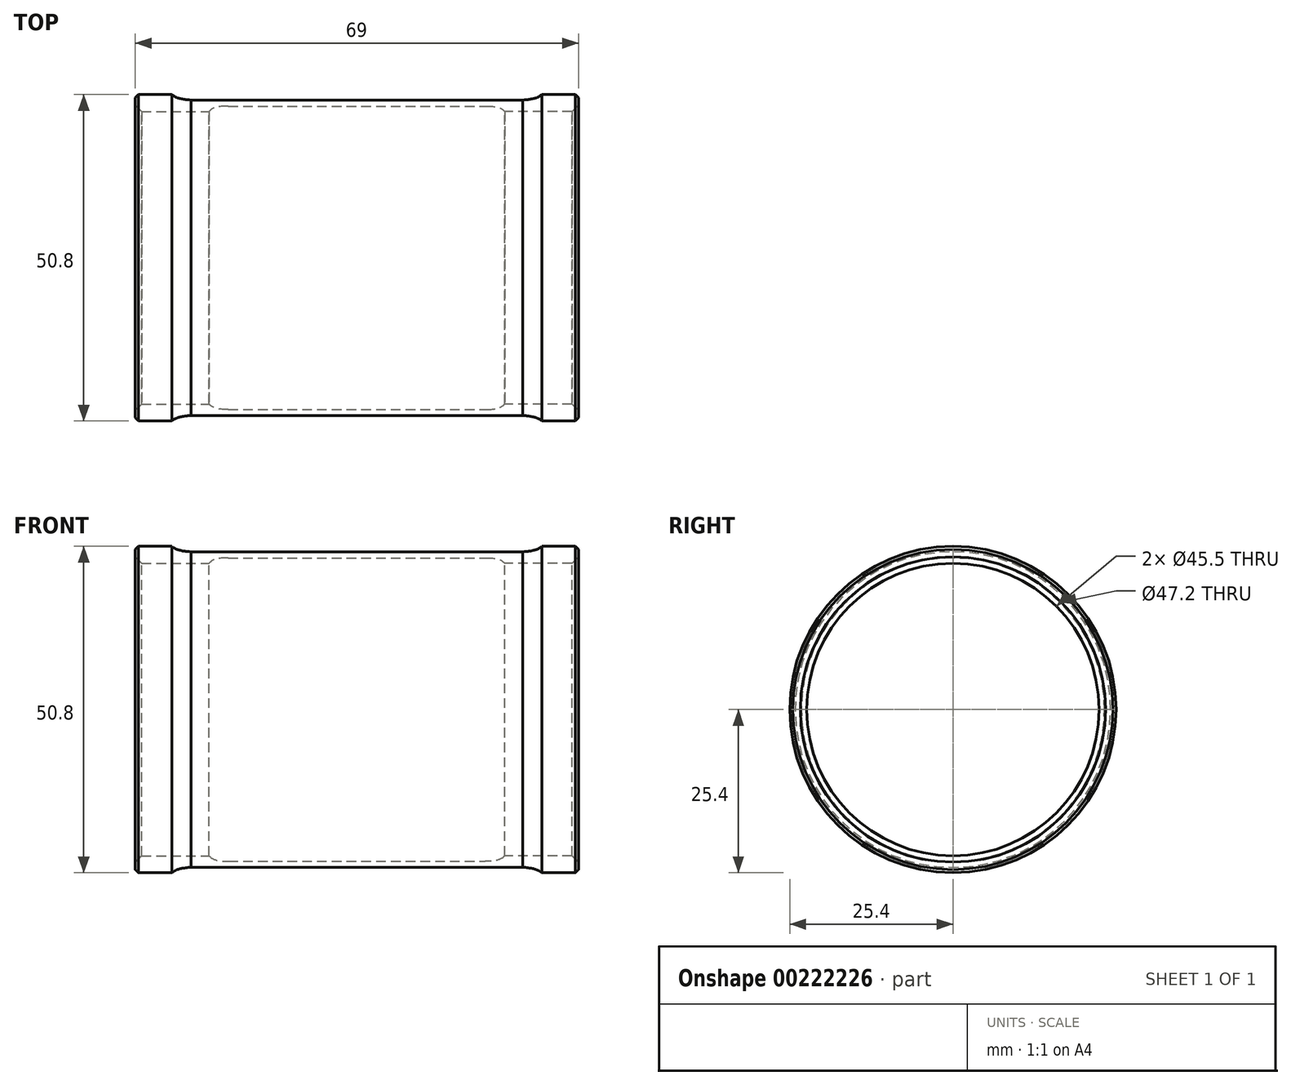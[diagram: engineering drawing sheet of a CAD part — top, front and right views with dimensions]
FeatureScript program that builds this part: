
annotation { "Feature Type Name" : "Feature", "Feature Type Description" : "" }
export const myFeature = defineFeature(function(context is Context, id is Id, definition is map)
    precondition{}
    {
        {
            var Q0;
            Q0=qCreatedBy(makeId("Top.planeOp"),FACE);
            var sketch = newSketch(context, id + "F0", { "sketchPlane" : qUnion([Q0])});
            skLineSegment(sketch, "E0.bottom", {"start": v(-34.5, -25.4) * mm, "end": v(-25.8, -25.4) * mm});
            skLineSegment(sketch, "E0.top", {"start": v(-34.5, 25.4) * mm, "end": v(-28.8, 25.4) * mm});
            skLineSegment(sketch, "E0.left", {"start": v(-34.5, -25.4) * mm, "end": v(-34.5, 25.4) * mm});
            skLineSegment(sketch, "E0.right", {"start": v(-25.8, -25.4) * mm, "end": v(-25.8, 22.75) * mm});
            skLineSegment(sketch, "E1.bottom", {"start": v(-34.5, -22.75) * mm, "end": v(-25.8, -22.75) * mm});
            skLineSegment(sketch, "E1.top", {"start": v(-34.5, 22.75) * mm, "end": v(-25.8, 22.75) * mm});
            skLineSegment(sketch, "E2", {"start": v(-20, 23.6) * mm, "end": v(0, 23.6) * mm});
            skLineSegment(sketch, "E3", {"start": v(0, 0) * mm, "end": v(0, 29.78) * mm});
            skLineSegment(sketch, "E4", {"start": v(-25.8, 24.55) * mm, "end": v(0, 24.55) * mm});
            skLineSegment(sketch, "E5", {"start": v(0, 0) * mm, "end": v(-67.86, 0) * mm, "construction": true});
            skPoint(sketch, "E5.endSnap0", {"position": v(-25.8, 0) * mm});
            skPoint(sketch, "E6", {"position": v(-28.8, 25.4) * mm});
            skFitSpline(sketch, "E7", {"points": [v(-28.8, 25.4) * mm, v(-25.8, 24.55) * mm], "startDerivative": vector(1.21, -1.2) * mm, "endDerivative": vector(5.4, -0.3) * mm});
            skLineSegment(sketch, "E8", {"start": v(-34.5, 22.75) * mm, "end": v(-23, 22.75) * mm});
            skFitSpline(sketch, "E9", {"points": [v(-23, 22.75) * mm, v(-20, 23.6) * mm], "startDerivative": vector(1.57, 2.03) * mm, "endDerivative": vector(4.6, 0) * mm});
            skSolve(sketch);
        }
        {
            var Q0;
            {var subQ0=sQuery(id+"F0.wireOp",EDGE,"E2");Q0=makeQuery(id+"F0.imprint","IMPRINT",FACE,{"disambiguationData":[TD([[makeQuery(id+"F0.imprint","IMPRINT",EDGE,{"derivedFrom":subQ0}),1.0]])]});}
            var Q1;
            {var subQ5=sQuery(id+"F0.wireOp",EDGE,"E0.top");Q1=makeQuery(id+"F0.imprint","IMPRINT",FACE,{"disambiguationData":[TD([[makeQuery(id+"F0.imprint","IMPRINT",EDGE,{"derivedFrom":subQ5}),-1.0]])]});}
            var Q2;
            Q2=sQuery(id+"F0.wireOp",EDGE,"E5");
            revolve(context, id + "F1", {"entities" : qUnion([Q0, Q1]), "axis" : qUnion([Q2]), "revolveType" : RevolveType.FULL});
        }
        {
            var Q0;
            Q0=makeQuery(id+"F1.opRevolve","SWEPT_EDGE",EDGE,{"disambiguationData":[OSD([sQuery(id+"F0.wireOp",EDGE,"E0.top"),sQuery(id+"F0.wireOp",EDGE,"E0.left")])]});
            chamfer(context, id + "F2", {"entities" : qUnion([Q0]), "width" : .5 * mm, "tangentPropagation" : true});
        }
        {
            var Q0;
            Q0=makeQuery(id+"F1.opRevolve","SWEPT_EDGE",EDGE,{"disambiguationData":[OSD([sQuery(id+"F0.wireOp",EDGE,"E0.left"),sQuery(id+"F0.wireOp",EDGE,"E1.top")])]});
            chamfer(context, id + "F3", {"entities" : qUnion([Q0]), "width" : 1 * mm, "tangentPropagation" : true});
        }
        {
            var Q0;
            Q0=makeQuery(id+"F1.opRevolve","SWEPT_BODY",BODY,{"disambiguationData":[OSD([sQuery(id+"F0.wireOp",EDGE,"E0.top"),sQuery(id+"F0.wireOp",EDGE,"E0.left"),sQuery(id+"F0.wireOp",EDGE,"E2"),sQuery(id+"F0.wireOp",EDGE,"E3"),sQuery(id+"F0.wireOp",EDGE,"E4"),sQuery(id+"F0.wireOp",EDGE,"E7"),sQuery(id+"F0.wireOp",EDGE,"E8"),sQuery(id+"F0.wireOp",EDGE,"E9")])]});
            var Q1;
            Q1=makeQuery(id+"F1.opRevolve","SWEPT_FACE",FACE,{"disambiguationData":[OSD([sQuery(id+"F0.wireOp",EDGE,"E3")])]});
            mirror(context, id + "F4", {"operationType" : NewBodyOperationType.ADD, "entities" : qUnion([Q0]), "mirrorPlane" : qUnion([Q1])});
        }
    });
